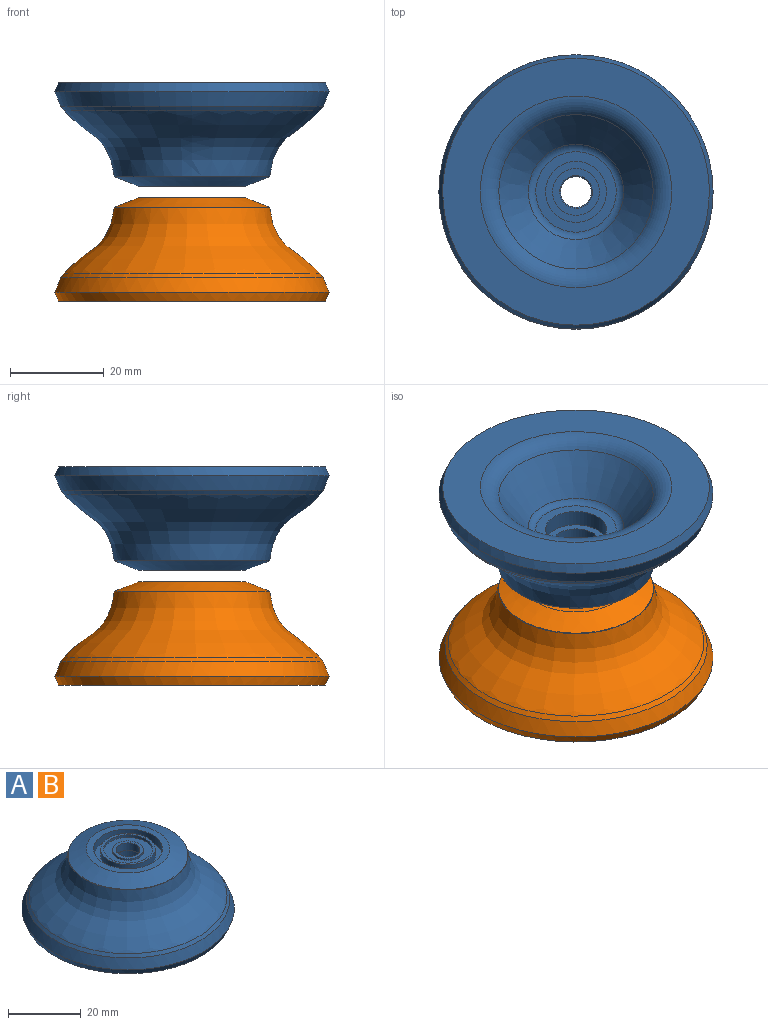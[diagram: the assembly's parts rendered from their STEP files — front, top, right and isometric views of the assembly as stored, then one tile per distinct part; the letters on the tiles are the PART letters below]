
ASSEMBLY  parts=2 mates=1
PART A: 26 faces, bbox 58.5x58.5x22 mm
  f0: cone r=28mm half-angle=37.4deg, axis (0,0,-1), area 12.1mm2, adj f24,f25
  f1: cylinder r=3.3mm len=6.6mm, axis (0,0,1), area 51.8mm2, adj f20,f22
  f2: cylinder r=4.25mm len=8.5mm, axis (0,0,1), area 16mm2, adj f17,f20
  f3: plane 56.92x56.92mm, normal (0,0,-1), area 1231.4mm2, adj f15,f23
  f4: plane 23x23mm, normal (0,0,1), area 131.9mm2, adj f9,f24
  f5: cone r=28mm half-angle=37.4deg, axis (0,0,-1), area 205mm2, adj f6,f25
  f6: cone r=30mm half-angle=21.8deg, axis (0,0,-1), area 608.9mm2, adj f5,f23
  f7: cone r=19.26mm half-angle=37.4deg, axis (0,0,-1), area 869.4mm2, adj f15,f21
  f8: plane 17.15x17.15mm, normal (0,0,-1), area 98.3mm2, adj f14,f21
  f9: cylinder r=9.5mm len=19mm, axis (0,0,1), area 149.2mm2, adj f4,f10
  f10: plane 19x19mm, normal (0,0,1), area 106.8mm2, adj f9,f11
  f11: cylinder r=7.5mm len=15mm, axis (0,0,1), area 117.8mm2, adj f10,f12
  f12: plane 15x15mm, normal (0,0,1), area 33.6mm2, adj f11,f16
  f13: plane 13x13mm, normal (0,0,-1), area 54.2mm2, adj f14,f19
  f14: cylinder r=6.5mm len=13mm, axis (0,0,-1), area 142.9mm2, adj f8,f13
  f15: torus R=20.45mm, axis (0,0,-1), area 528mm2, adj f3,f7
  f16: cylinder r=6.75mm len=13.5mm, axis (0,0,1), area 38.2mm2, adj f12,f17
  f17: plane 13.5x13.5mm, normal (0,0,1), area 86.4mm2, adj f2,f16
  f18: plane 10x10mm, normal (0,0,-1), area 40.1mm2, adj f19,f22
  f19: cylinder r=5mm len=10mm, axis (0,0,-1), area 141.4mm2, adj f13,f18
  f20: plane 8.5x8.5mm, normal (0,0,1), area 22.5mm2, adj f1,f2
  f21: torus R=8.58mm, axis (0,0,1), area 108.8mm2, adj f7,f8
  f22: cone r=3.5mm half-angle=45deg, axis (0,0,-1), area 6mm2, adj f1,f18
  f23: cone r=28.46mm half-angle=23.2deg, axis (0,0,1), area 366.3mm2, adj f3,f6
  f24: cone r=16.52mm half-angle=68.4deg, axis (0,0,-1), area 475.1mm2, adj f0,f4
  f25: revolved ~54.57x54.57mm, area 2404mm2, adj f0,f5
PART B: same geometry as A
PLACE A rot(axis=(1,0,0),180deg) t=(35.49,29.38,26.87)mm
PLACE B t=(35.49,29.38,24.33)mm
MATE fastened A.f1 <-> B.f21  axis (0,0,-1) through (35.49,29.38,26.87)mm
